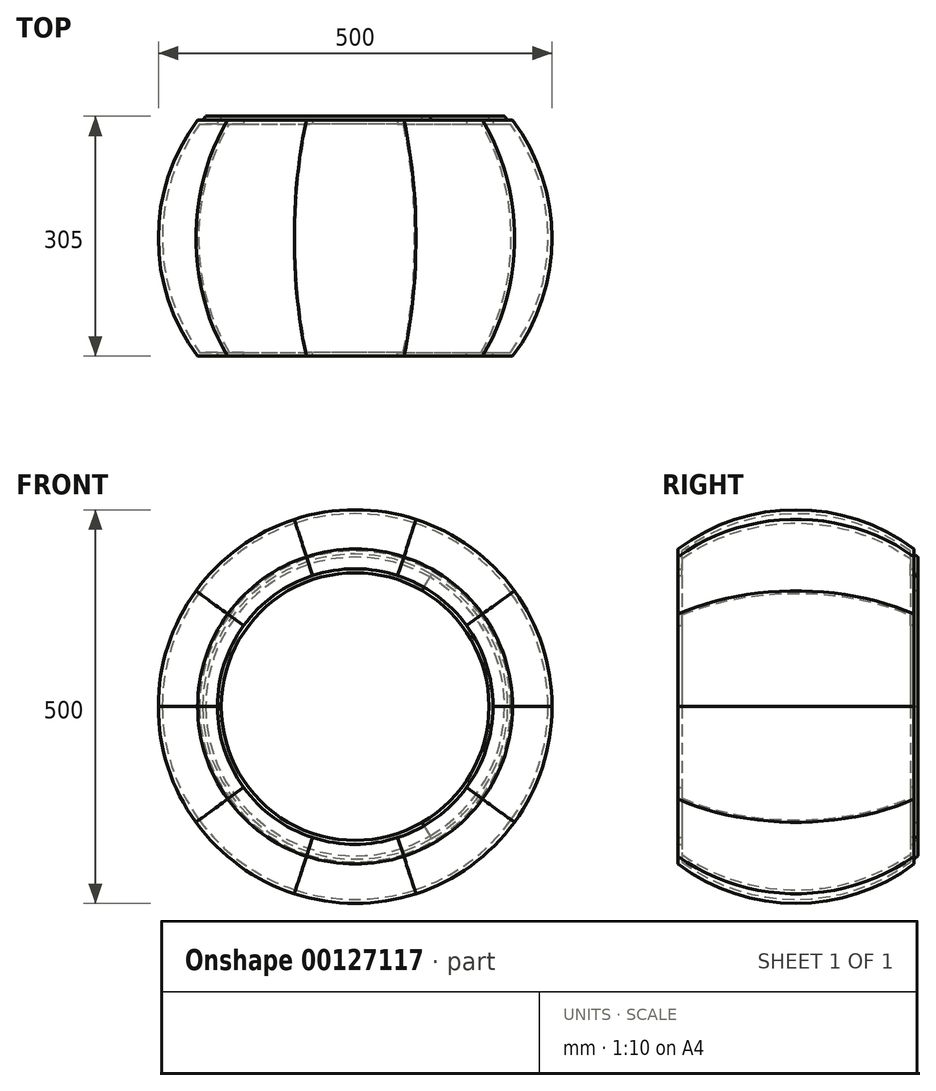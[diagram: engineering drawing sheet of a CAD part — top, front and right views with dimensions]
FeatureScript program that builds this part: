
annotation { "Feature Type Name" : "Feature", "Feature Type Description" : "" }
export const myFeature = defineFeature(function(context is Context, id is Id, definition is map)
    precondition{}
    {
        {
            var Q0;
            Q0=qCreatedBy(makeId("Top.planeOp"),FACE);
            var sketch = newSketch(context, id + "F0", { "sketchPlane" : qUnion([Q0])});
            skArc(sketch, "E0", {"start": v(0, 250) * mm, "mid": v(250, 0) * mm, "end": v(0, -250) * mm});
            skLineSegment(sketch, "E1", {"start": v(0, 250) * mm, "end": v(0, -250) * mm});
            skLineSegment(sketch, "E2", {"start": v(0, 150) * mm, "end": v(200, 150) * mm});
            skLineSegment(sketch, "E3", {"start": v(0, -150) * mm, "end": v(200, -150) * mm});
            skArc(sketch, "E4", {"start": v(0, 245) * mm, "mid": v(107.88, 219.97) * mm, "end": v(193.71, 150) * mm});
            skLineSegment(sketch, "E5", {"start": v(175, 150) * mm, "end": v(175, 145) * mm});
            skLineSegment(sketch, "E6", {"start": v(175, 145) * mm, "end": v(197.48, 145) * mm});
            skArc(sketch, "E7.trimOffspring", {"start": v(197.48, 145) * mm, "mid": v(245, 0) * mm, "end": v(197.48, -145) * mm});
            skLineSegment(sketch, "E8", {"start": v(175, -150) * mm, "end": v(175, -145) * mm});
            skLineSegment(sketch, "E9", {"start": v(175, -145) * mm, "end": v(197.48, -145) * mm});
            skArc(sketch, "E10.trimOffspring", {"start": v(193.71, -150) * mm, "mid": v(107.88, -219.97) * mm, "end": v(0, -245) * mm});
            skArc(sketch, "E11", {"start": v(0, 240) * mm, "mid": v(101, 217.72) * mm, "end": v(183.23, 155) * mm});
            skLineSegment(sketch, "E12", {"start": v(170, 150) * mm, "end": v(170, 155) * mm});
            skLineSegment(sketch, "E13", {"start": v(170, 155) * mm, "end": v(189.74, 155) * mm});
            skSolve(sketch);
        }
        {
            var Q0;
            {var subQ7=sQuery(id+"F0.wireOp",EDGE,"E5");Q0=makeQuery(id+"F0.imprint","IMPRINT",FACE,{"disambiguationData":[TD([[makeQuery(id+"F0.imprint","IMPRINT",EDGE,{"derivedFrom":subQ7}),1.0]])]});}
            var Q1;
            Q1=sQuery(id+"F0.wireOp",EDGE,"E1");
            revolve(context, id + "F1", {"entities" : qUnion([Q0]), "axis" : qUnion([Q1]), "revolveType" : RevolveType.ONE_DIRECTION, "angle" : 36 * degree});
        }
        {
            var Q0;
            {var subQ5=sQuery(id+"F0.wireOp",EDGE,"E12");Q0=makeQuery(id+"F0.imprint","IMPRINT",FACE,{"disambiguationData":[TD([[makeQuery(id+"F0.imprint","IMPRINT",EDGE,{"derivedFrom":subQ5}),-1.0]])]});}
            var Q1;
            Q1=sQuery(id+"F0.wireOp",EDGE,"E1");
            revolve(context, id + "F2", {"entities" : qUnion([Q0]), "axis" : qUnion([Q1]), "revolveType" : RevolveType.TWO_DIRECTIONS, "angle" : 60 * degree, "angleBack" : 300 * degree});
        }
        {
            var Q0;
            Q0=makeQuery(id+"F1.opRevolve","SWEPT_BODY",BODY,{"disambiguationData":[OSD([sQuery(id+"F0.wireOp",EDGE,"E0"),sQuery(id+"F0.wireOp",EDGE,"E2"),sQuery(id+"F0.wireOp",EDGE,"E3"),sQuery(id+"F0.wireOp",EDGE,"E5"),sQuery(id+"F0.wireOp",EDGE,"E6"),sQuery(id+"F0.wireOp",EDGE,"E7.trimOffspring"),sQuery(id+"F0.wireOp",EDGE,"E8"),sQuery(id+"F0.wireOp",EDGE,"E9")])]});
            var Q1;
            Q1=sQuery(id+"F0.wireOp",EDGE,"E1");
            circularPattern(context, id + "F3", {"entities" : qUnion([Q0]), "axis" : qUnion([Q1]), "angle" : 36 * degree, "instanceCount" : 10});
        }
        {
            var Q0;
            Q0=makeQuery(id+"F2.opRevolve","SWEPT_BODY",BODY,{"disambiguationData":[OSD([sQuery(id+"F0.wireOp",EDGE,"E2"),sQuery(id+"F0.wireOp",EDGE,"E4"),sQuery(id+"F0.wireOp",EDGE,"E12"),sQuery(id+"F0.wireOp",EDGE,"E13")])]});
            var Q1;
            Q1=sQuery(id+"F0.wireOp",EDGE,"E1");
            circularPattern(context, id + "F4", {"entities" : qUnion([Q0]), "axis" : qUnion([Q1]), "angle" : 120 * degree, "instanceCount" : 3});
        }
    });
